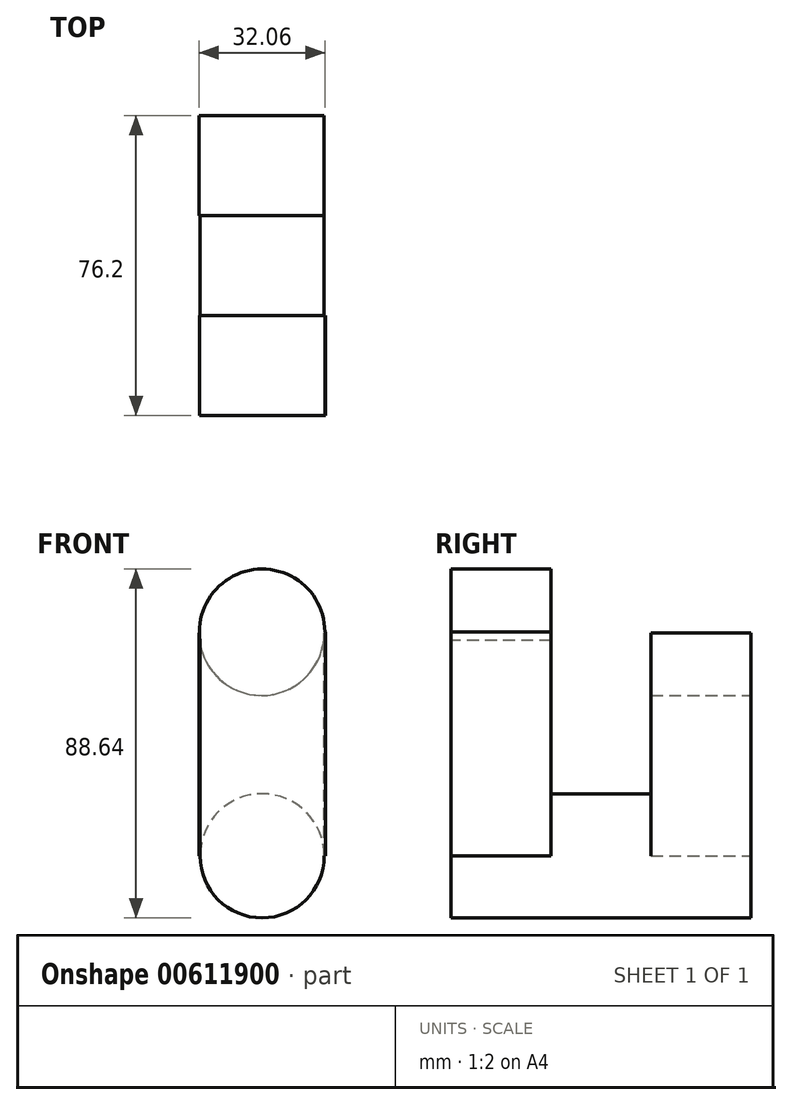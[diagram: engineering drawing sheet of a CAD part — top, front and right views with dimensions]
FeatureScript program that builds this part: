
annotation { "Feature Type Name" : "Feature", "Feature Type Description" : "" }
export const myFeature = defineFeature(function(context is Context, id is Id, definition is map)
    precondition{}
    {
        {
            var Q0;
            Q0=qCreatedBy(makeId("Front.planeOp"),FACE);
            var sketch = newSketch(context, id + "F0", { "sketchPlane" : qUnion([Q0])});
            skCircle(sketch, "E0", {"center": v(0, 0) * mm, "radius": 15.76 * mm});
            skSolve(sketch);
        }
        {
            var Q0;
            Q0=makeQuery(id+"F0.imprint","IMPRINT",FACE,{"disambiguationData":[TD([[makeQuery(id+"F0.imprint","IMPRINT",EDGE,{"derivedFrom":sQuery(id+"F0.wireOp",EDGE,"E0")}),1.0]])]});
            extrude(context, id + "F1", {"entities" : qUnion([Q0]), "depth" : 38.1 * mm, "offsetDistance" : 25.4 * mm});
        }
        {
            var Q0;
            Q0=makeQuery(id+"F1.opExtrude","CAP_FACE",FACE,{"disambiguationData":[OSD([sQuery(id+"F0.wireOp",EDGE,"E0")])],"isStart":true});
            extrude(context, id + "F2", {"entities" : qUnion([Q0]), "operationType" : NewBodyOperationType.ADD, "depth" : 38.1 * mm, "offsetDistance" : 25.4 * mm});
        }
        {
            var Q0;
            Q0=makeQuery(id+"F1.opExtrude","CAP_FACE",FACE,{"disambiguationData":[OSD([sQuery(id+"F0.wireOp",EDGE,"E0")])],"isStart":false});
            var sketch = newSketch(context, id + "F3", { "sketchPlane" : qUnion([Q0])});
            skLineSegment(sketch, "E1.bottom", {"start": v(-15.76, 0) * mm, "end": v(16.03, 0) * mm});
            skLineSegment(sketch, "E1.top", {"start": v(-15.76, 56.95) * mm, "end": v(16.03, 56.95) * mm});
            skLineSegment(sketch, "E1.left", {"start": v(-15.76, 0) * mm, "end": v(-15.76, 56.95) * mm});
            skLineSegment(sketch, "E1.right", {"start": v(16.03, 0) * mm, "end": v(16.03, 56.95) * mm});
            skSolve(sketch);
        }
        {
            var Q0;
            Q0=makeQuery(id+"F3.imprint","IMPRINT",FACE,{"disambiguationData":[TD([[makeQuery(id+"F3.imprint","IMPRINT",EDGE,{"derivedFrom":sQuery(id+"F3.wireOp",EDGE,"E1.top")}),-1.0]])]});
            var sketch = newSketch(context, id + "F4", { "sketchPlane" : qUnion([Q0])});
            skCircle(sketch, "E2", {"center": v(0, 56.95) * mm, "radius": 15.92 * mm});
            skSolve(sketch);
        }
        {
            var Q0;
            Q0=makeQuery(id+"F2.opExtrude","CAP_FACE",FACE,{"disambiguationData":[OSD([sQuery(id+"F0.wireOp",EDGE,"E0")])],"isStart":false});
            var sketch = newSketch(context, id + "F5", { "sketchPlane" : qUnion([Q0])});
            skLineSegment(sketch, "E3.bottom", {"start": v(-15.76, 0) * mm, "end": v(16.03, 0) * mm});
            skLineSegment(sketch, "E3.top", {"start": v(-15.76, 56.65) * mm, "end": v(16.03, 56.65) * mm});
            skLineSegment(sketch, "E3.left", {"start": v(-15.76, 0) * mm, "end": v(-15.76, 56.65) * mm});
            skLineSegment(sketch, "E3.right", {"start": v(16.03, 0) * mm, "end": v(16.03, 56.65) * mm});
            skCircle(sketch, "E4", {"center": v(0.13, 56.65) * mm, "radius": 15.9 * mm});
            skSolve(sketch);
        }
        {
            var Q0;
            {var subQ1=sQuery(id+"F5.wireOp",EDGE,"E3.left");Q0=makeQuery(id+"F5.imprint","IMPRINT",FACE,{"disambiguationData":[TD([[makeQuery(id+"F5.imprint","IMPRINT",EDGE,{"derivedFrom":subQ1}),-1.0]])]});}
            extrude(context, id + "F6", {"entities" : qUnion([Q0]), "operationType" : NewBodyOperationType.ADD, "oppositeDirection" : true, "depth" : 25.4 * mm, "offsetDistance" : 25.4 * mm});
        }
        {
            var Q0;
            Q0=makeQuery(id+"F3.imprint","IMPRINT",FACE,{"disambiguationData":[TD([[makeQuery(id+"F3.imprint","IMPRINT",EDGE,{"derivedFrom":sQuery(id+"F3.wireOp",EDGE,"E1.top")}),-1.0]])]});
            extrude(context, id + "F7", {"entities" : qUnion([Q0]), "operationType" : NewBodyOperationType.ADD, "oppositeDirection" : true, "depth" : 25.4 * mm, "offsetDistance" : 25.4 * mm});
        }
        {
            var Q0;
            {var subQ0=sQuery(id+"F4.wireOp",EDGE,"E2");var subQ1=makeQuery(id+"F3.imprint","IMPRINT",EDGE,{"derivedFrom":sQuery(id+"F3.wireOp",EDGE,"E1.top")});var subQ2=makeQuery(id+"F4.imprint","INTERSECT",VERTEX,{"derivedFrom":[subQ1,subQ0]});Q0=makeQuery(id+"F4.imprint","IMPRINT",FACE,{"disambiguationData":[TD([[makeQuery(id+"F4.imprint","IMPRINT",EDGE,{"disambiguationData":[TD([[subQ2,-1.0]])],"derivedFrom":subQ0}),1.0]])]});}
            extrude(context, id + "F8", {"entities" : qUnion([Q0]), "operationType" : NewBodyOperationType.ADD, "oppositeDirection" : true, "depth" : 25.4 * mm, "offsetDistance" : 25.4 * mm});
        }
    });
